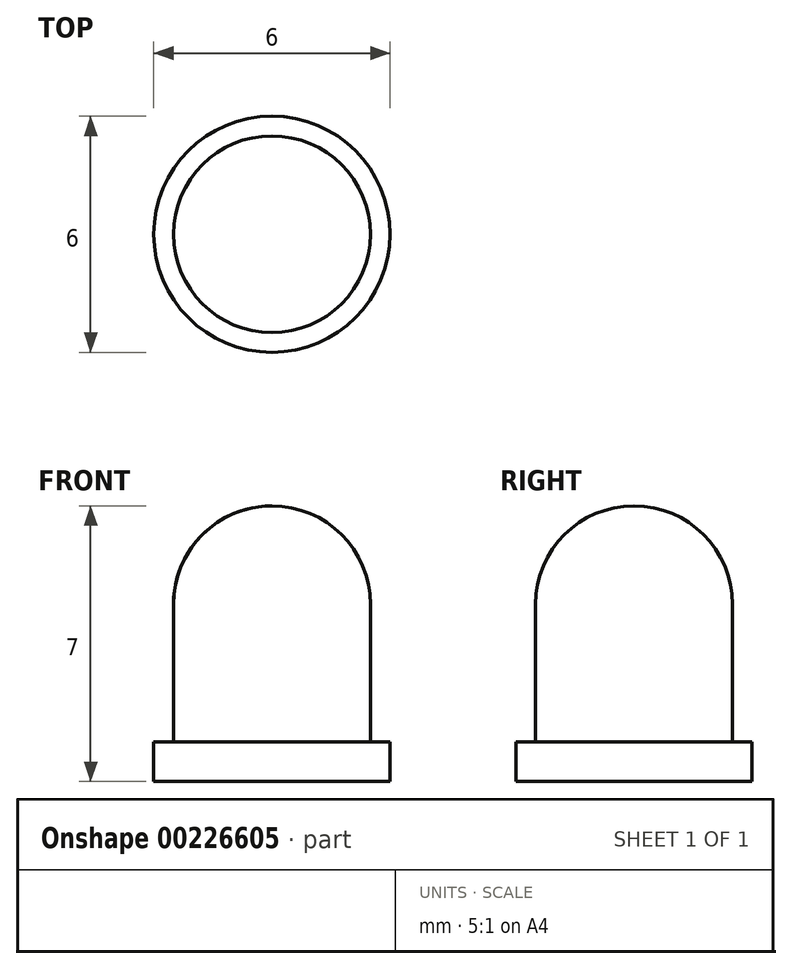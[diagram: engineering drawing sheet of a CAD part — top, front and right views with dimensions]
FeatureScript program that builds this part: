
annotation { "Feature Type Name" : "Feature", "Feature Type Description" : "" }
export const myFeature = defineFeature(function(context is Context, id is Id, definition is map)
    precondition{}
    {
        {
            var Q0;
            Q0=qCreatedBy(makeId("Front.planeOp"),FACE);
            var sketch = newSketch(context, id + "F0", { "sketchPlane" : qUnion([Q0])});
            skLineSegment(sketch, "E0", {"start": v(0, 0) * mm, "end": v(-3, 0) * mm});
            skLineSegment(sketch, "E1", {"start": v(-3, 0) * mm, "end": v(-3, 1) * mm});
            skLineSegment(sketch, "E2", {"start": v(-3, 1) * mm, "end": v(-2.5, 1) * mm});
            skLineSegment(sketch, "E3", {"start": v(0, 7) * mm, "end": v(0, 0) * mm});
            skLineSegment(sketch, "E4", {"start": v(-2.5, 1) * mm, "end": v(-2.5, 4.5) * mm});
            skArc(sketch, "E5", {"start": v(-2.5, 4.5) * mm, "mid": v(-1.77, 6.27) * mm, "end": v(0, 7) * mm});
            skArc(sketch, "E6.MirrorCS", {"start": v(2.5, 4.5) * mm, "mid": v(1.77, 6.27) * mm, "end": v(0, 7) * mm, "construction": true});
            skLineSegment(sketch, "E7.MirrorCS", {"start": v(2.5, 1) * mm, "end": v(2.5, 4.5) * mm, "construction": true});
            skLineSegment(sketch, "E8.MirrorCS", {"start": v(3, 1) * mm, "end": v(2.5, 1) * mm, "construction": true});
            skLineSegment(sketch, "E9.MirrorCS", {"start": v(3, 0) * mm, "end": v(3, 1) * mm, "construction": true});
            skLineSegment(sketch, "E10.MirrorCS", {"start": v(0, 0) * mm, "end": v(3, 0) * mm, "construction": true});
            skSolve(sketch);
        }
        {
            var Q0;
            Q0 = qSketchRegion(id + "F0", true);
            var Q1;
            Q1=sQuery(id+"F0.wireOp",EDGE,"E3");
            revolve(context, id + "F1", {"entities" : qUnion([Q0]), "axis" : qUnion([Q1]), "revolveType" : RevolveType.ONE_DIRECTION, "angle" : 360 * degree});
        }
    });
